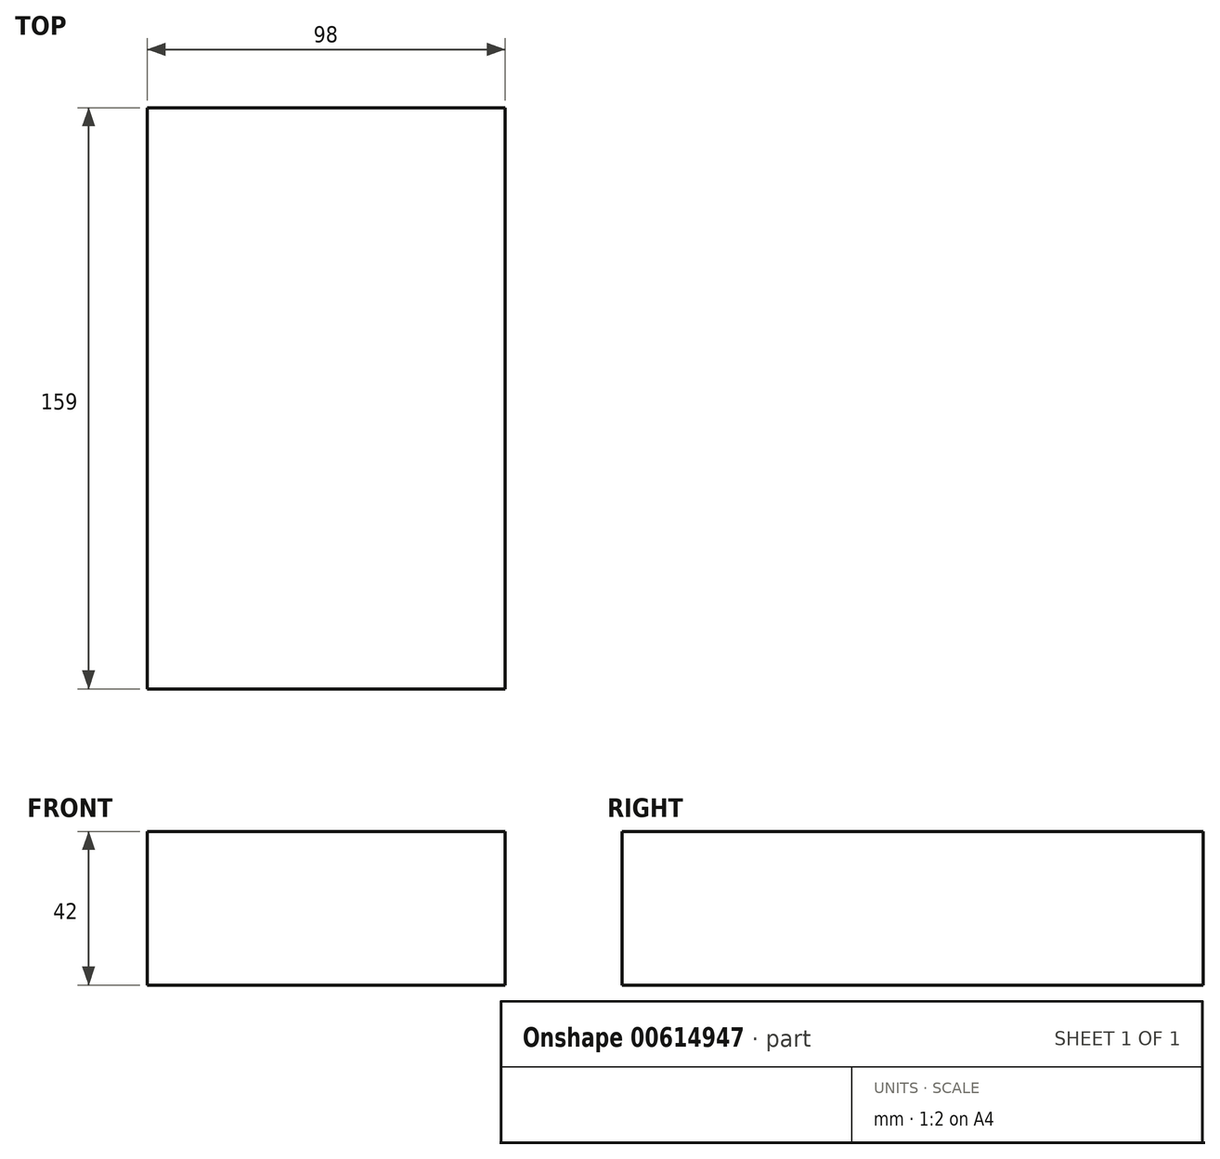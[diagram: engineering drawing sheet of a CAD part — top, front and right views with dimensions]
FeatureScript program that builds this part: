
annotation { "Feature Type Name" : "Feature", "Feature Type Description" : "" }
export const myFeature = defineFeature(function(context is Context, id is Id, definition is map)
    precondition{}
    {
        {
            var Q0;
            Q0=qCreatedBy(makeId("Top.planeOp"),FACE);
            var sketch = newSketch(context, id + "F0", { "sketchPlane" : qUnion([Q0])});
            skLineSegment(sketch, "E0.bottom", {"start": v(49, 79.5) * mm, "end": v(-49, 79.5) * mm});
            skLineSegment(sketch, "E0.top", {"start": v(49, -79.5) * mm, "end": v(-49, -79.5) * mm});
            skLineSegment(sketch, "E0.left", {"start": v(49, 79.5) * mm, "end": v(49, -79.5) * mm});
            skLineSegment(sketch, "E0.right", {"start": v(-49, 79.5) * mm, "end": v(-49, -79.5) * mm});
            skPoint(sketch, "E0.middle", {"position": v(0, 0) * mm});
            skSolve(sketch);
        }
        {
            var Q0;
            Q0 = qSketchRegion(id + "F0", true);
            extrude(context, id + "F1", {"entities" : qUnion([Q0]), "depth" : 42 * mm, "offsetDistance" : 25 * mm});
        }
    });
